# Revit family: 277V DOBLE 5630 IP 65_S25120.U.1
name_source: partatom
category: Luminarias
units: mm (PartAtom-declared; Revit-internal decimal feet)

## family parameters
Compartido = No
Corte con vacíos al cargar = No
Cota de conector redondo = Diámetro de uso
Origen de luz = Sí
Punto de cálculo de habitación = No
Se basa en plano de trabajo = Sí
Siempre vertical = No
Tipo de pieza = Normal

## types (1)
- 277V DOBLE 5630 IP 65_S25120.U.1
    Archivo de red fotométrica = S25120.U.1_277V DOBLE 5630 IP65.IES
    Cambio de temperatura de color de luz atenuada = <Ninguno>
    Comentarios de vataje = 277V
    Costo = 0 $
    Descripción = TIRA LED DOBLE DE PCB CON RECUBRIMIENTO DE PLASTICO 21MM MONOCROMATICA , CON UNA POTENCIA DE 19.80W/M DE UN TIPO DE LED 5630 SMD, USO PARA INTERIORES COMO EXTERIORES IP65, IRC80, 120 LEDS POR METRO, PRESENTACION DE 50M, TEMPERATURA EN BLANCO ULTRA CALIDO 2400K, 1324.6 LUMENES POR METRO, EFICIENCIA DE 67 LM/W, CORTE A 50CM, ALIMENTADA A 277V, REQUIERE ACCESORIOS COMO CONVERTIDOR DE CORRIENTE (1 POR SEGMENTO DE TIRA), CONECTOR INTERMEDIO (CONSIDERAR EN CORTES DE TIRA O ANGULOS CERRADOS), CONECTOR AGUJA (CONSIDERAR 1PZA PRO CADA CONVERTIDOR), FUNDA TERMOCONTRACTIL (CONSIDERAR 2PZAS POR SEGMENTO DE TIRA), TAPA FINAL (CONSIDERAR 1PZA POR SEGMENTO DE TIRA) Y CLIPS DE SUJECION (CONSIDERAR 4 PZAS POR 1M)
    Elevación por defecto = 0 mm  [stored 0 ft]
    Fabricante = BRILLANT
    Filtro de color = 16777215
    Longitud de línea de emisión = 600 mm  [stored 1.9685 ft]
    Lámpara = 5630 SMD
    Modelo = S25120.U.1
    Ángulo de inclinación = 60.00°

note: [stored X ft] marks values corroborated as IEEE doubles in the binary element streams (Revit-internal decimal feet)

## geometry (parser evidence)
native form markers: Blend x2
no freeform markers — native parametric forms only
